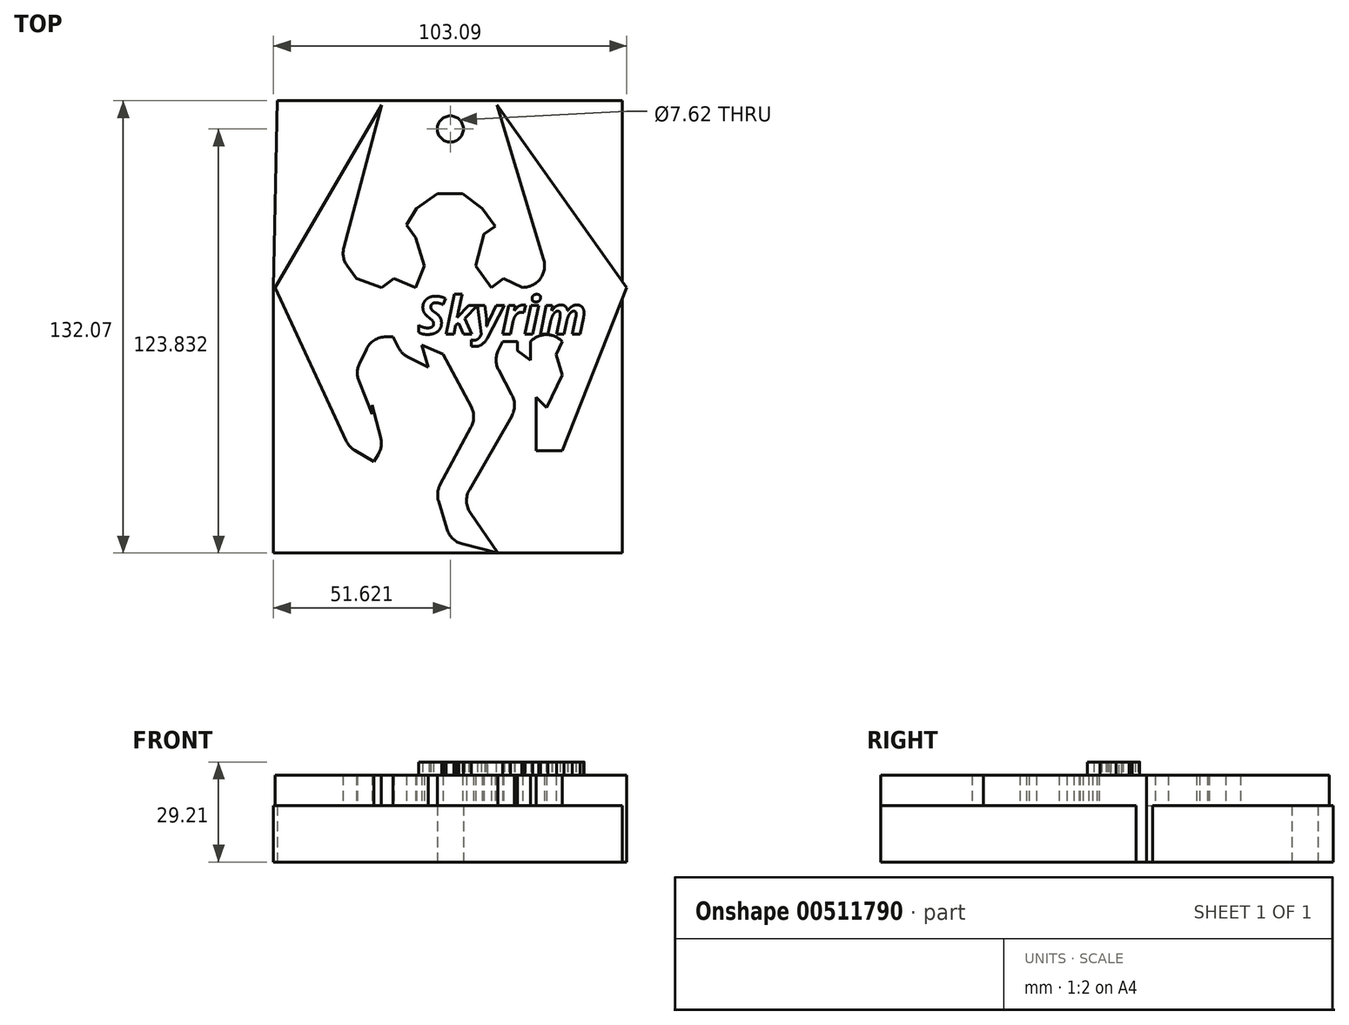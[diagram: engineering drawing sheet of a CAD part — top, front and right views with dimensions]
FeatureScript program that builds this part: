
annotation { "Feature Type Name" : "Feature", "Feature Type Description" : "" }
export const myFeature = defineFeature(function(context is Context, id is Id, definition is map)
    precondition{}
    {
        {
            var Q0;
            Q0=qCreatedBy(makeId("Top.planeOp"),FACE);
            var sketch = newSketch(context, id + "F0", { "sketchPlane" : qUnion([Q0])});
            skLineSegment(sketch, "E0", {"start": v(-26.94, 0) * mm, "end": v(17.58, 0) * mm});
            skLineSegment(sketch, "E1", {"start": v(23.66, 8.18) * mm, "end": v(10.07, 53.34) * mm});
            skLineSegment(sketch, "E2", {"start": v(10.07, 53.34) * mm, "end": v(47.9, 0) * mm});
            skLineSegment(sketch, "E3", {"start": v(47.9, 0) * mm, "end": v(29.12, -47.63) * mm});
            skLineSegment(sketch, "E4", {"start": v(29.12, -47.63) * mm, "end": v(21.5, -47.63) * mm});
            skLineSegment(sketch, "E5", {"start": v(21.5, -47.63) * mm, "end": v(21.5, -32.11) * mm});
            skLineSegment(sketch, "E6", {"start": v(21.5, -32.11) * mm, "end": v(24.5, -35.1) * mm});
            skLineSegment(sketch, "E7", {"start": v(24.5, -35.1) * mm, "end": v(29.12, -25.58) * mm});
            skLineSegment(sketch, "E8", {"start": v(29.12, -25.58) * mm, "end": v(27.34, -19.67) * mm});
            skLineSegment(sketch, "E9", {"start": v(27.34, -19.67) * mm, "end": v(29.12, -15.78) * mm});
            skLineSegment(sketch, "E10", {"start": v(29.12, -15.78) * mm, "end": v(28.98, -15.65) * mm});
            skLineSegment(sketch, "E11", {"start": v(20, -15.65) * mm, "end": v(19.87, -15.78) * mm});
            skPoint(sketch, "E12.visualSharp", {"position": v(26.13, 0) * mm});
            skArc(sketch, "E12.filletArc", {"start": v(17.58, 0) * mm, "mid": v(22.68, 2.56) * mm, "end": v(23.66, 8.18) * mm});
            skLineSegment(sketch, "E13", {"start": v(19.87, -15.78) * mm, "end": v(19.87, -21.23) * mm});
            skLineSegment(sketch, "E14", {"start": v(19.87, -21.23) * mm, "end": v(16.06, -18.5) * mm});
            skPoint(sketch, "E14.endSnap0", {"position": v(19.87, -18.5) * mm});
            skLineSegment(sketch, "E15", {"start": v(16.06, -18.5) * mm, "end": v(16.06, -15.78) * mm});
            skLineSegment(sketch, "E16", {"start": v(16.06, -15.78) * mm, "end": v(11.7, -15.78) * mm});
            skLineSegment(sketch, "E17", {"start": v(11.7, -15.78) * mm, "end": v(10.44, -18.3) * mm});
            skLineSegment(sketch, "E18", {"start": v(10.51, -24.12) * mm, "end": v(14.41, -31.47) * mm});
            skPoint(sketch, "E19.visualSharp", {"position": v(24.5, -11.16) * mm});
            skArc(sketch, "E19.filletArc", {"start": v(28.98, -15.65) * mm, "mid": v(24.5, -13.79) * mm, "end": v(20, -15.65) * mm});
            skPoint(sketch, "E20.visualSharp", {"position": v(8.98, -21.23) * mm});
            skArc(sketch, "E20.filletArc", {"start": v(10.44, -18.3) * mm, "mid": v(9.77, -21.22) * mm, "end": v(10.51, -24.12) * mm});
            skLineSegment(sketch, "E21", {"start": v(14.32, -37.6) * mm, "end": v(1.99, -59.12) * mm});
            skLineSegment(sketch, "E22", {"start": v(2.28, -65.89) * mm, "end": v(10.34, -77.56) * mm});
            skLineSegment(sketch, "E23", {"start": v(10.34, -77.56) * mm, "end": v(-0.06, -74.9) * mm});
            skLineSegment(sketch, "E24", {"start": v(-4.57, -70.59) * mm, "end": v(-7.02, -62.46) * mm});
            skLineSegment(sketch, "E25", {"start": v(-6.53, -57.63) * mm, "end": v(2.48, -40.81) * mm});
            skLineSegment(sketch, "E26", {"start": v(2.5, -34.84) * mm, "end": v(-5.66, -19.47) * mm});
            skLineSegment(sketch, "E27", {"start": v(-5.66, -19.47) * mm, "end": v(-11.97, -16.87) * mm});
            skLineSegment(sketch, "E28", {"start": v(-11.97, -16.87) * mm, "end": v(-10.05, -23.26) * mm});
            skLineSegment(sketch, "E29", {"start": v(-10.05, -23.26) * mm, "end": v(-15.86, -20.38) * mm});
            skLineSegment(sketch, "E30", {"start": v(-18.65, -17.67) * mm, "end": v(-20.36, -14.44) * mm});
            skPoint(sketch, "E31.visualSharp", {"position": v(0, -62.6) * mm});
            skArc(sketch, "E31.filletArc", {"start": v(1.99, -59.12) * mm, "mid": v(1.16, -62.54) * mm, "end": v(2.28, -65.89) * mm});
            skPoint(sketch, "E32.visualSharp", {"position": v(-3.54, -74.02) * mm});
            skArc(sketch, "E32.filletArc", {"start": v(-4.57, -70.59) * mm, "mid": v(-2.88, -73.34) * mm, "end": v(-0.06, -74.9) * mm});
            skPoint(sketch, "E33.visualSharp", {"position": v(-7.78, -59.94) * mm});
            skArc(sketch, "E33.filletArc", {"start": v(-6.53, -57.63) * mm, "mid": v(-7.26, -60) * mm, "end": v(-7.02, -62.46) * mm});
            skPoint(sketch, "E34.visualSharp", {"position": v(4.08, -37.83) * mm});
            skArc(sketch, "E34.filletArc", {"start": v(2.48, -40.81) * mm, "mid": v(3.24, -37.83) * mm, "end": v(2.5, -34.84) * mm});
            skPoint(sketch, "E35.visualSharp", {"position": v(16.06, -34.56) * mm});
            skArc(sketch, "E35.filletArc", {"start": v(14.32, -37.6) * mm, "mid": v(15.15, -34.55) * mm, "end": v(14.41, -31.47) * mm});
            skPoint(sketch, "E36.visualSharp", {"position": v(-17.69, -19.47) * mm});
            skArc(sketch, "E36.filletArc", {"start": v(-18.65, -17.67) * mm, "mid": v(-17.47, -19.24) * mm, "end": v(-15.86, -20.38) * mm});
            skLineSegment(sketch, "E37", {"start": v(17.58, 0) * mm, "end": v(11.97, 2.56) * mm});
            skPoint(sketch, "E37.endSnap0", {"position": v(22.68, 2.56) * mm});
            skLineSegment(sketch, "E38", {"start": v(11.97, 2.56) * mm, "end": v(8.36, 0) * mm});
            skLineSegment(sketch, "E39", {"start": v(8.36, 0) * mm, "end": v(3.86, 6.35) * mm});
            skLineSegment(sketch, "E40", {"start": v(3.86, 6.35) * mm, "end": v(6.26, 15.51) * mm});
            skLineSegment(sketch, "E41", {"start": v(6.26, 15.51) * mm, "end": v(9.5, 17.81) * mm});
            skLineSegment(sketch, "E42", {"start": v(9.5, 17.81) * mm, "end": v(5.78, 23.07) * mm});
            skLineSegment(sketch, "E43", {"start": v(5.78, 23.07) * mm, "end": v(0, 27.37) * mm});
            skLineSegment(sketch, "E44", {"start": v(0, 27.37) * mm, "end": v(-7.35, 27.37) * mm});
            skLineSegment(sketch, "E45", {"start": v(-7.35, 27.37) * mm, "end": v(-13.42, 23.07) * mm});
            skLineSegment(sketch, "E46", {"start": v(-13.42, 23.07) * mm, "end": v(-16.33, 18.23) * mm});
            skLineSegment(sketch, "E47", {"start": v(-16.33, 18.23) * mm, "end": v(-13.73, 14.57) * mm});
            skLineSegment(sketch, "E48", {"start": v(-13.73, 14.57) * mm, "end": v(-11.16, 6.35) * mm});
            skLineSegment(sketch, "E49", {"start": v(-11.16, 6.35) * mm, "end": v(-13.73, 0) * mm});
            skLineSegment(sketch, "E50", {"start": v(-13.73, 0) * mm, "end": v(-20.05, 2.56) * mm});
            skLineSegment(sketch, "E51", {"start": v(-20.05, 2.56) * mm, "end": v(-23.66, 0) * mm});
            skLineSegment(sketch, "E52", {"start": v(-23.66, 0) * mm, "end": v(-31.02, 2.56) * mm});
            skLineSegment(sketch, "E53", {"start": v(-31.02, 2.56) * mm, "end": v(-33.7, 6.34) * mm});
            skLineSegment(sketch, "E54", {"start": v(-34.66, 11.63) * mm, "end": v(-23.66, 53.34) * mm});
            skLineSegment(sketch, "E55", {"start": v(-23.66, 53.34) * mm, "end": v(-54.7, 0) * mm});
            skLineSegment(sketch, "E56", {"start": v(-54.7, 0) * mm, "end": v(-34.03, -44.74) * mm});
            skLineSegment(sketch, "E57", {"start": v(-31.5, -47.54) * mm, "end": v(-25.85, -50.9) * mm});
            skLineSegment(sketch, "E58", {"start": v(-25.85, -50.9) * mm, "end": v(-24.61, -48.8) * mm});
            skLineSegment(sketch, "E59", {"start": v(-23.92, -44) * mm, "end": v(-26.4, -34.3) * mm});
            skLineSegment(sketch, "E60", {"start": v(-26.4, -34.3) * mm, "end": v(-26.4, -37.01) * mm});
            skLineSegment(sketch, "E61", {"start": v(-26.4, -37.01) * mm, "end": v(-30.27, -27.34) * mm});
            skLineSegment(sketch, "E62", {"start": v(-30.1, -22.26) * mm, "end": v(-28.12, -18.07) * mm});
            skLineSegment(sketch, "E63", {"start": v(-22.38, -14.44) * mm, "end": v(-20.36, -14.44) * mm});
            skPoint(sketch, "E64.visualSharp", {"position": v(-35.42, 8.76) * mm});
            skArc(sketch, "E64.filletArc", {"start": v(-34.66, 11.63) * mm, "mid": v(-34.77, 8.88) * mm, "end": v(-33.7, 6.34) * mm});
            skPoint(sketch, "E65.visualSharp", {"position": v(-31.3, -24.77) * mm});
            skArc(sketch, "E65.filletArc", {"start": v(-30.1, -22.26) * mm, "mid": v(-30.72, -24.78) * mm, "end": v(-30.27, -27.34) * mm});
            skPoint(sketch, "E66.visualSharp", {"position": v(-26.4, -14.44) * mm});
            skArc(sketch, "E66.filletArc", {"start": v(-22.38, -14.44) * mm, "mid": v(-25.78, -15.43) * mm, "end": v(-28.12, -18.07) * mm});
            skPoint(sketch, "E67.visualSharp", {"position": v(-33.2, -46.54) * mm});
            skArc(sketch, "E67.filletArc", {"start": v(-34.03, -44.74) * mm, "mid": v(-32.98, -46.34) * mm, "end": v(-31.5, -47.54) * mm});
            skPoint(sketch, "E68.visualSharp", {"position": v(-23.27, -46.54) * mm});
            skArc(sketch, "E68.filletArc", {"start": v(-24.61, -48.8) * mm, "mid": v(-23.8, -46.46) * mm, "end": v(-23.92, -44) * mm});
            skSolve(sketch);
        }
        {
            var Q0;
            Q0 = qSketchRegion(id + "F0", true);
            extrude(context, id + "F1", {"entities" : qUnion([Q0]), "depth" : 25.4 * mm});
        }
        {
            var Q0;
            Q0=qCreatedBy(makeId("Top.planeOp"),FACE);
            var sketch = newSketch(context, id + "F2", { "sketchPlane" : qUnion([Q0])});
            skLineSegment(sketch, "E69", {"start": v(-55.19, 0) * mm, "end": v(-55.19, -77.56) * mm});
            skLineSegment(sketch, "E70", {"start": v(-55.19, -77.56) * mm, "end": v(46.68, -77.56) * mm});
            skLineSegment(sketch, "E71", {"start": v(46.68, -77.56) * mm, "end": v(46.68, 54.5) * mm});
            skLineSegment(sketch, "E72", {"start": v(46.68, 54.5) * mm, "end": v(-54.1, 54.5) * mm});
            skLineSegment(sketch, "E73", {"start": v(-54.1, 54.5) * mm, "end": v(-55.19, 0) * mm});
            skSolve(sketch);
        }
        {
            var Q0;
            Q0 = qSketchRegion(id + "F2", true);
            extrude(context, id + "F3", {"entities" : qUnion([Q0]), "operationType" : NewBodyOperationType.ADD, "depth" : 16.5 * mm});
        }
        {
            var Q0;
            Q0=qCreatedBy(makeId("Top.planeOp"),FACE);
            var sketch = newSketch(context, id + "F4", { "sketchPlane" : qUnion([Q0])});
            skCircle(sketch, "E74", {"center": v(-3.57, 46.27) * mm, "radius": 3.35 * mm});
            skSolve(sketch);
        }
        {
            var Q0;
            Q0=sQuery(id+"F4.wireOp",VERTEX,"E74.center");
            var Q1;
            Q1=makeQuery(id+"F1.opExtrude","SWEPT_BODY",BODY,{"disambiguationData":[OSD([sQuery(id+"F0.wireOp",EDGE,"E1"),sQuery(id+"F0.wireOp",EDGE,"E2"),sQuery(id+"F0.wireOp",EDGE,"E3"),sQuery(id+"F0.wireOp",EDGE,"E4"),sQuery(id+"F0.wireOp",EDGE,"E5"),sQuery(id+"F0.wireOp",EDGE,"E6"),sQuery(id+"F0.wireOp",EDGE,"E7"),sQuery(id+"F0.wireOp",EDGE,"E8"),sQuery(id+"F0.wireOp",EDGE,"E9"),sQuery(id+"F0.wireOp",EDGE,"E10"),sQuery(id+"F0.wireOp",EDGE,"E11"),sQuery(id+"F0.wireOp",EDGE,"E12.filletArc"),sQuery(id+"F0.wireOp",EDGE,"E13"),sQuery(id+"F0.wireOp",EDGE,"E14"),sQuery(id+"F0.wireOp",EDGE,"E15"),sQuery(id+"F0.wireOp",EDGE,"E16"),sQuery(id+"F0.wireOp",EDGE,"E17"),sQuery(id+"F0.wireOp",EDGE,"E18"),sQuery(id+"F0.wireOp",EDGE,"E19.filletArc"),sQuery(id+"F0.wireOp",EDGE,"E20.filletArc"),sQuery(id+"F0.wireOp",EDGE,"E21"),sQuery(id+"F0.wireOp",EDGE,"E22"),sQuery(id+"F0.wireOp",EDGE,"E23"),sQuery(id+"F0.wireOp",EDGE,"E24"),sQuery(id+"F0.wireOp",EDGE,"E25"),sQuery(id+"F0.wireOp",EDGE,"E26"),sQuery(id+"F0.wireOp",EDGE,"E27"),sQuery(id+"F0.wireOp",EDGE,"E28"),sQuery(id+"F0.wireOp",EDGE,"E29"),sQuery(id+"F0.wireOp",EDGE,"E30"),sQuery(id+"F0.wireOp",EDGE,"E31.filletArc"),sQuery(id+"F0.wireOp",EDGE,"E32.filletArc"),sQuery(id+"F0.wireOp",EDGE,"E33.filletArc"),sQuery(id+"F0.wireOp",EDGE,"E34.filletArc"),sQuery(id+"F0.wireOp",EDGE,"E35.filletArc"),sQuery(id+"F0.wireOp",EDGE,"E36.filletArc"),sQuery(id+"F0.wireOp",EDGE,"E37"),sQuery(id+"F0.wireOp",EDGE,"E38"),sQuery(id+"F0.wireOp",EDGE,"E39"),sQuery(id+"F0.wireOp",EDGE,"E40"),sQuery(id+"F0.wireOp",EDGE,"E41"),sQuery(id+"F0.wireOp",EDGE,"E42"),sQuery(id+"F0.wireOp",EDGE,"E43"),sQuery(id+"F0.wireOp",EDGE,"E44"),sQuery(id+"F0.wireOp",EDGE,"E45"),sQuery(id+"F0.wireOp",EDGE,"E46"),sQuery(id+"F0.wireOp",EDGE,"E47"),sQuery(id+"F0.wireOp",EDGE,"E48"),sQuery(id+"F0.wireOp",EDGE,"E49"),sQuery(id+"F0.wireOp",EDGE,"E50"),sQuery(id+"F0.wireOp",EDGE,"E51"),sQuery(id+"F0.wireOp",EDGE,"E52"),sQuery(id+"F0.wireOp",EDGE,"E53"),sQuery(id+"F0.wireOp",EDGE,"E54"),sQuery(id+"F0.wireOp",EDGE,"E55"),sQuery(id+"F0.wireOp",EDGE,"E56"),sQuery(id+"F0.wireOp",EDGE,"E57"),sQuery(id+"F0.wireOp",EDGE,"E58"),sQuery(id+"F0.wireOp",EDGE,"E59"),sQuery(id+"F0.wireOp",EDGE,"E60"),sQuery(id+"F0.wireOp",EDGE,"E61"),sQuery(id+"F0.wireOp",EDGE,"E62"),sQuery(id+"F0.wireOp",EDGE,"E63"),sQuery(id+"F0.wireOp",EDGE,"E64.filletArc"),sQuery(id+"F0.wireOp",EDGE,"E65.filletArc"),sQuery(id+"F0.wireOp",EDGE,"E66.filletArc"),sQuery(id+"F0.wireOp",EDGE,"E67.filletArc"),sQuery(id+"F0.wireOp",EDGE,"E68.filletArc")])]});
            hole(context, id + "F5", {"style" : HoleStyle.SIMPLE, "endStyle" : HoleEndStyle.THROUGH, "oppositeDirection" : true, "holeDiameter" : 7.62 * mm, "isTappedThrough" : true, "tappedDepth" : 12.7 * mm, "tapClearance" : 3, "locations" : qUnion([Q0]), "scope" : qUnion([Q1])});
        }
        {
            var Q0;
            Q0=qCreatedBy(makeId("Top.planeOp"),FACE);
            var sketch = newSketch(context, id + "F6", { "sketchPlane" : qUnion([Q0])});
            skText(sketch, "E75", { "text": "Skyrim", "fontName": "OpenSans-BoldItalic.ttf"});
            const initialGuessF6  = {"E75": [-0.01318, -0.01359, 1, 0, 0.01098]};
            skSetInitialGuess(sketch, initialGuessF6);
            skSolve(sketch);
        }
        {
            var Q0;
            Q0 = qSketchRegion(id + "F6", true);
            extrude(context, id + "F7", {"entities" : qUnion([Q0]), "operationType" : NewBodyOperationType.ADD, "depth" : 29.2 * mm});
        }
    });
